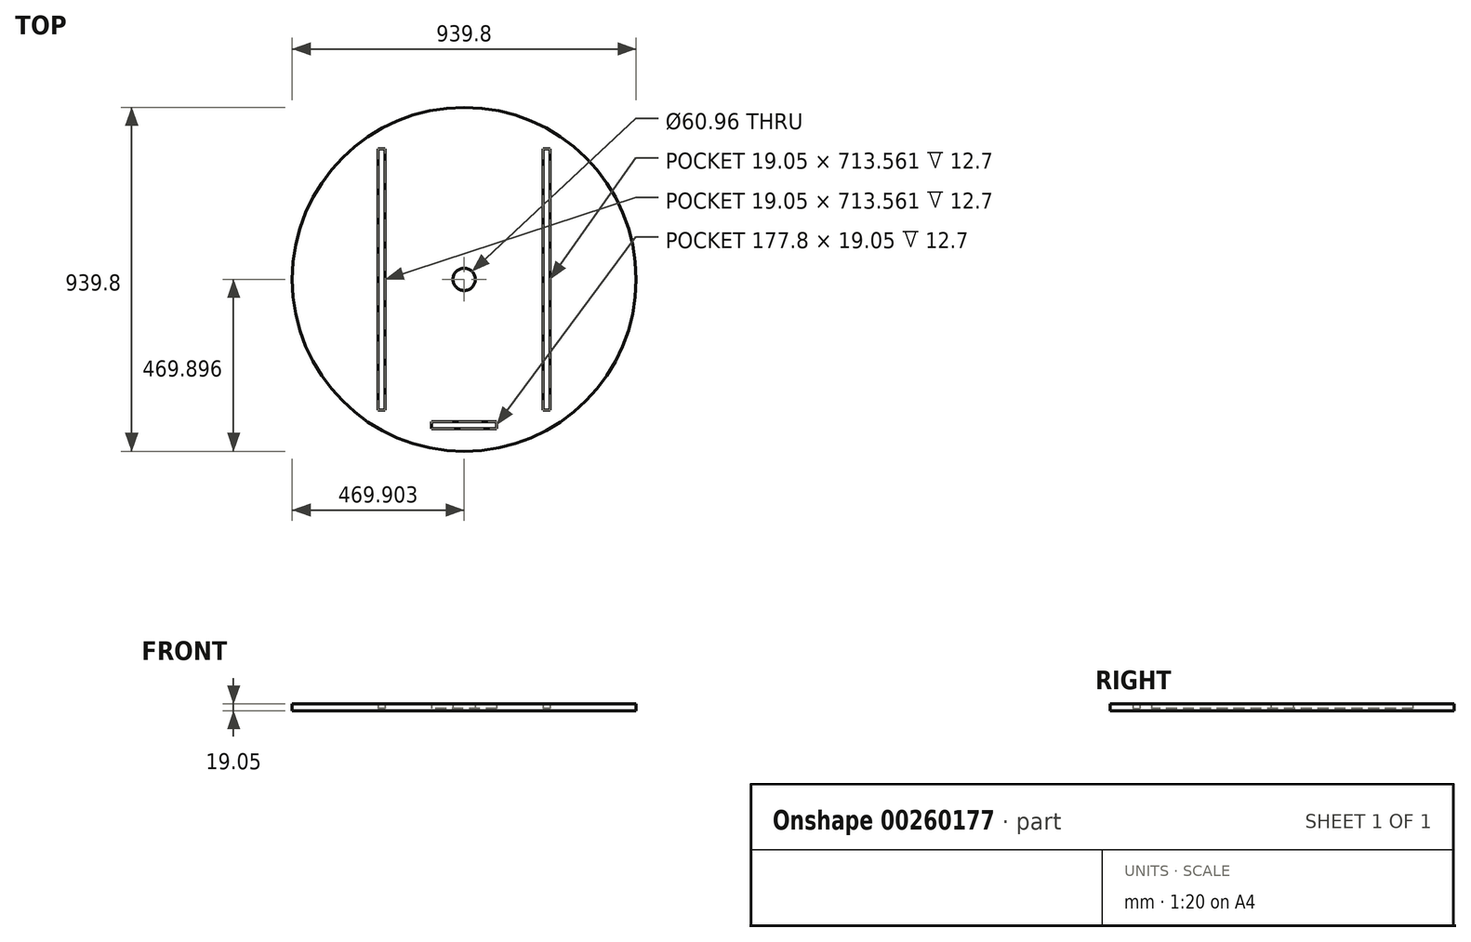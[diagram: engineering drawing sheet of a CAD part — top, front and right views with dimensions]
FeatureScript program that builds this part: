
annotation { "Feature Type Name" : "Feature", "Feature Type Description" : "" }
export const myFeature = defineFeature(function(context is Context, id is Id, definition is map)
    precondition{}
    {
        {
            var Q0;
            Q0=qCreatedBy(makeId("Top.planeOp"),FACE);
            var sketch = newSketch(context, id + "F0", { "sketchPlane" : qUnion([Q0])});
            skCircle(sketch, "E0", {"center": v(-57.05, 15.93) * mm, "radius": 469.9 * mm});
            skLineSegment(sketch, "E1", {"start": v(-292, 15.93) * mm, "end": v(-292, 362.55) * mm});
            skLineSegment(sketch, "E2", {"start": v(-292, 362.55) * mm, "end": v(-292, -330.7) * mm});
            skPoint(sketch, "E3.orphan", {"position": v(-526.95, 15.93) * mm});
            skLineSegment(sketch, "E4.MirrorCS", {"start": v(177.9, 362.55) * mm, "end": v(177.9, -330.7) * mm});
            skLineSegment(sketch, "E5.right", {"start": v(177.9, 15.93) * mm, "end": v(177.9, -330.7) * mm});
            skPoint(sketch, "E5.bottom.start.orphan", {"position": v(-292, 422.87) * mm});
            skPoint(sketch, "E6.orphan", {"position": v(177.9, 422.87) * mm});
            skPoint(sketch, "E7.orphan", {"position": v(177.9, -391.02) * mm});
            skPoint(sketch, "E8.orphan", {"position": v(-292, -391.02) * mm});
            skLineSegment(sketch, "E9.0", {"start": v(-272.95, 362.55) * mm, "end": v(-272.95, -330.7) * mm});
            skLineSegment(sketch, "E10.0", {"start": v(158.85, 362.55) * mm, "end": v(158.85, -330.7) * mm});
            skCircle(sketch, "E11", {"center": v(-57.05, 15.93) * mm, "radius": 30.48 * mm});
            skLineSegment(sketch, "E12.top", {"start": v(177.9, -340.85) * mm, "end": v(158.85, -340.85) * mm});
            skLineSegment(sketch, "E12.left", {"start": v(177.9, -330.7) * mm, "end": v(177.9, -340.85) * mm});
            skLineSegment(sketch, "E12.right", {"start": v(158.85, -330.7) * mm, "end": v(158.85, -340.85) * mm});
            skLineSegment(sketch, "E13.top", {"start": v(177.9, 372.7) * mm, "end": v(158.85, 372.7) * mm});
            skLineSegment(sketch, "E13.left", {"start": v(177.9, 362.55) * mm, "end": v(177.9, 372.7) * mm});
            skLineSegment(sketch, "E13.right", {"start": v(158.85, 362.55) * mm, "end": v(158.85, 372.7) * mm});
            skLineSegment(sketch, "E14.top", {"start": v(-272.95, 372.7) * mm, "end": v(-292, 372.7) * mm});
            skLineSegment(sketch, "E14.left", {"start": v(-272.95, 362.55) * mm, "end": v(-272.95, 372.7) * mm});
            skLineSegment(sketch, "E14.right", {"start": v(-292, 362.55) * mm, "end": v(-292, 372.7) * mm});
            skLineSegment(sketch, "E15.top", {"start": v(-272.95, -340.85) * mm, "end": v(-292, -340.85) * mm});
            skLineSegment(sketch, "E15.left", {"start": v(-272.95, -330.7) * mm, "end": v(-272.95, -340.85) * mm});
            skLineSegment(sketch, "E15.right", {"start": v(-292, -330.7) * mm, "end": v(-292, -340.85) * mm});
            skLineSegment(sketch, "E16", {"start": v(158.85, -340.85) * mm, "end": v(-272.95, -340.85) * mm});
            skLineSegment(sketch, "E17", {"start": v(-57.05, -340.85) * mm, "end": v(-57.05, -391.65) * mm});
            skPoint(sketch, "E17.endSnap0", {"position": v(-57.05, -340.85) * mm});
            skLineSegment(sketch, "E18.bottom", {"start": v(-57.05, -391.65) * mm, "end": v(31.85, -391.65) * mm});
            skLineSegment(sketch, "E18.top", {"start": v(-57.05, -372.6) * mm, "end": v(31.85, -372.6) * mm});
            skLineSegment(sketch, "E18.left", {"start": v(-57.05, -391.65) * mm, "end": v(-57.05, -372.6) * mm});
            skLineSegment(sketch, "E18.right", {"start": v(31.85, -391.65) * mm, "end": v(31.85, -372.6) * mm});
            skLineSegment(sketch, "E19.bottom", {"start": v(-57.05, -391.65) * mm, "end": v(-145.95, -391.65) * mm});
            skLineSegment(sketch, "E19.top", {"start": v(-57.05, -372.6) * mm, "end": v(-145.95, -372.6) * mm});
            skLineSegment(sketch, "E19.right", {"start": v(-145.95, -391.65) * mm, "end": v(-145.95, -372.6) * mm});
            skSolve(sketch);
        }
        {
            var Q0;
            Q0 = qSketchRegion(id + "F0", true);
            extrude(context, id + "F1", {"entities" : qUnion([Q0]), "depth" : 19.05 * mm});
        }
        {
            var Q0;
            Q0=makeQuery(id+"F1.opExtrude","CAP_FACE",FACE,{"disambiguationData":[OSD([sQuery(id+"F0.wireOp",EDGE,"E0"),sQuery(id+"F0.wireOp",EDGE,"E4.MirrorCS"),sQuery(id+"F0.wireOp",EDGE,"E2"),sQuery(id+"F0.wireOp",EDGE,"E5.right"),sQuery(id+"F0.wireOp",EDGE,"E9.0"),sQuery(id+"F0.wireOp",EDGE,"E10.0"),sQuery(id+"F0.wireOp",EDGE,"E11"),sQuery(id+"F0.wireOp",EDGE,"E12.top"),sQuery(id+"F0.wireOp",EDGE,"E12.left"),sQuery(id+"F0.wireOp",EDGE,"E12.right"),sQuery(id+"F0.wireOp",EDGE,"E13.top"),sQuery(id+"F0.wireOp",EDGE,"E13.left"),sQuery(id+"F0.wireOp",EDGE,"E13.right"),sQuery(id+"F0.wireOp",EDGE,"E14.top"),sQuery(id+"F0.wireOp",EDGE,"E14.left"),sQuery(id+"F0.wireOp",EDGE,"E14.right"),sQuery(id+"F0.wireOp",EDGE,"E15.top"),sQuery(id+"F0.wireOp",EDGE,"E15.left"),sQuery(id+"F0.wireOp",EDGE,"E15.right")])],"isStart":true});
            var sketch = newSketch(context, id + "F2", { "sketchPlane" : qUnion([Q0])});
            skLineSegment(sketch, "E20.bottom", {"start": v(177.9, 340.85) * mm, "end": v(158.85, 340.85) * mm});
            skLineSegment(sketch, "E20.left", {"start": v(177.9, 340.85) * mm, "end": v(177.9, -372.7) * mm});
            skLineSegment(sketch, "E20.right", {"start": v(158.85, 340.85) * mm, "end": v(158.85, -372.7) * mm});
            skLineSegment(sketch, "E21.bottom", {"start": v(-272.95, 340.85) * mm, "end": v(-292, 340.85) * mm});
            skLineSegment(sketch, "E21.left", {"start": v(-272.95, 340.85) * mm, "end": v(-272.95, -372.7) * mm});
            skLineSegment(sketch, "E21.right", {"start": v(-292, 340.85) * mm, "end": v(-292, -372.7) * mm});
            skLineSegment(sketch, "E22.top", {"start": v(-272.95, -372.7) * mm, "end": v(-292, -372.7) * mm});
            skLineSegment(sketch, "E23.top", {"start": v(177.9, -372.7) * mm, "end": v(158.85, -372.7) * mm});
            skLineSegment(sketch, "E24.bottom", {"start": v(31.85, 391.65) * mm, "end": v(-145.95, 391.65) * mm});
            skLineSegment(sketch, "E24.top", {"start": v(31.85, 372.6) * mm, "end": v(-145.95, 372.6) * mm});
            skLineSegment(sketch, "E24.left", {"start": v(31.85, 391.65) * mm, "end": v(31.85, 372.6) * mm});
            skLineSegment(sketch, "E24.right", {"start": v(-145.95, 391.65) * mm, "end": v(-145.95, 372.6) * mm});
            skSolve(sketch);
        }
        {
            var Q0;
            Q0 = qSketchRegion(id + "F2", true);
            extrude(context, id + "F3", {"entities" : qUnion([Q0]), "operationType" : NewBodyOperationType.ADD, "oppositeDirection" : true, "depth" : 6.35 * mm});
        }
    });
